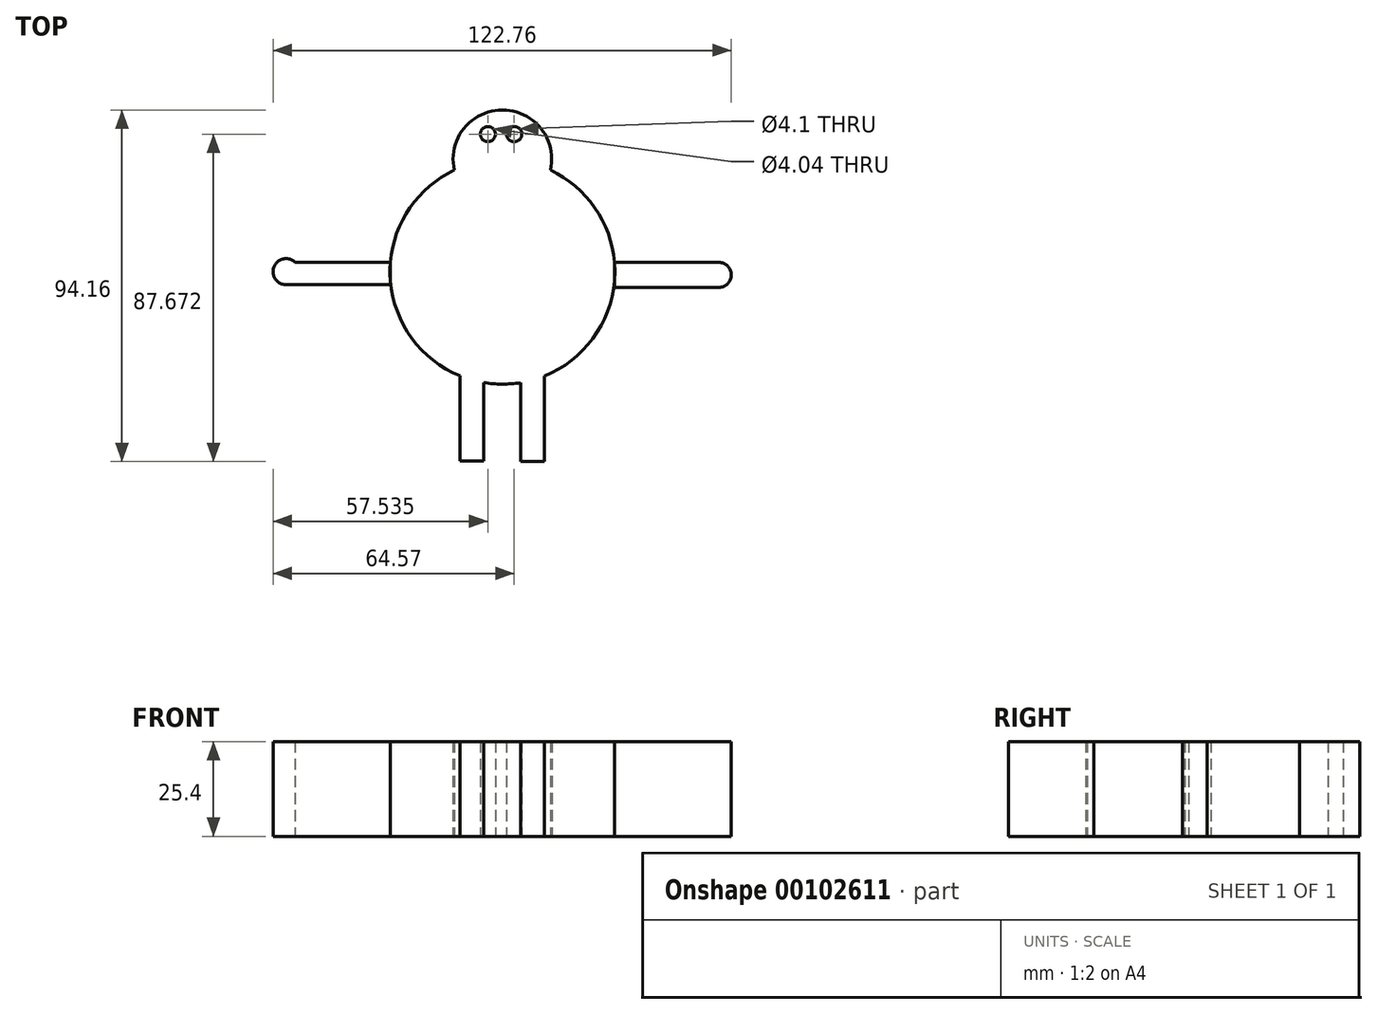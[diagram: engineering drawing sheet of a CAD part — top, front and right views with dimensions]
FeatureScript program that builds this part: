
annotation { "Feature Type Name" : "Feature", "Feature Type Description" : "" }
export const myFeature = defineFeature(function(context is Context, id is Id, definition is map)
    precondition{}
    {
        {
            var Q0;
            Q0=qCreatedBy(makeId("Top.planeOp"),FACE);
            var sketch = newSketch(context, id + "F0", { "sketchPlane" : qUnion([Q0])});
            skCircle(sketch, "E0", {"center": v(0, 0) * mm, "radius": 30.12 * mm});
            skCircle(sketch, "E1", {"center": v(0, 30.12) * mm, "radius": 13.21 * mm});
            skLineSegment(sketch, "E2.bottom", {"start": v(-30.02, 2.48) * mm, "end": v(-57.96, 2.48) * mm});
            skLineSegment(sketch, "E2.top", {"start": v(-30.02, -3.48) * mm, "end": v(-57.96, -3.48) * mm});
            skLineSegment(sketch, "E2.left", {"start": v(-30.02, 2.48) * mm, "end": v(-30.02, -3.48) * mm});
            skLineSegment(sketch, "E2.right", {"start": v(-57.96, 2.48) * mm, "end": v(-57.96, -3.48) * mm});
            skLineSegment(sketch, "E3.bottom", {"start": v(30.02, 2.48) * mm, "end": v(57.96, 2.48) * mm});
            skLineSegment(sketch, "E3.top", {"start": v(30.02, -4.23) * mm, "end": v(57.96, -4.23) * mm});
            skLineSegment(sketch, "E3.left", {"start": v(30.02, 2.48) * mm, "end": v(30.02, -4.23) * mm});
            skLineSegment(sketch, "E3.right", {"start": v(57.96, 2.48) * mm, "end": v(57.96, -4.23) * mm});
            skCircle(sketch, "E4", {"center": v(57.96, -0.87) * mm, "radius": 3.36 * mm});
            skCircle(sketch, "E5", {"center": v(-57.96, 0) * mm, "radius": 3.48 * mm});
            skLineSegment(sketch, "E6", {"start": v(-57.96, -3.48) * mm, "end": v(-60.96, -9.14) * mm});
            skLineSegment(sketch, "E7", {"start": v(-61.44, 0) * mm, "end": v(-67.56, -6.31) * mm});
            skPoint(sketch, "E7.endSnap0", {"position": v(-59.46, -6.31) * mm});
            skLineSegment(sketch, "E8", {"start": v(-61.44, 2.48) * mm, "end": v(-66.3, 5.59) * mm});
            skLineSegment(sketch, "E9", {"start": v(-57.96, 2.48) * mm, "end": v(-61.98, 11.43) * mm});
            skLineSegment(sketch, "E10", {"start": v(59.5, -3.85) * mm, "end": v(67.3, -11.43) * mm});
            skLineSegment(sketch, "E11", {"start": v(67.3, -11.43) * mm, "end": v(59.5, -3.85) * mm});
            skLineSegment(sketch, "E12", {"start": v(61.2, 0) * mm, "end": v(72.64, -7.87) * mm});
            skLineSegment(sketch, "E13", {"start": v(72.64, -7.87) * mm, "end": v(61.2, 0) * mm});
            skLineSegment(sketch, "E14", {"start": v(61.2, 0) * mm, "end": v(70.87, 6.86) * mm});
            skLineSegment(sketch, "E15", {"start": v(70.87, 6.86) * mm, "end": v(61.2, 0) * mm});
            skLineSegment(sketch, "E16", {"start": v(57.96, 2.48) * mm, "end": v(64.26, 12.2) * mm});
            skLineSegment(sketch, "E17", {"start": v(64.26, 12.2) * mm, "end": v(57.96, 2.48) * mm});
            skLineSegment(sketch, "E18.bottom", {"start": v(-11.35, -27.9) * mm, "end": v(-5, -27.9) * mm});
            skLineSegment(sketch, "E18.top", {"start": v(-11.35, -50.76) * mm, "end": v(-5, -50.76) * mm});
            skLineSegment(sketch, "E18.left", {"start": v(-11.35, -27.9) * mm, "end": v(-11.35, -50.76) * mm});
            skLineSegment(sketch, "E18.right", {"start": v(-5, -27.9) * mm, "end": v(-5, -50.76) * mm});
            skLineSegment(sketch, "E19.bottom", {"start": v(11.19, -27.97) * mm, "end": v(4.84, -27.97) * mm});
            skLineSegment(sketch, "E19.top", {"start": v(11.19, -50.83) * mm, "end": v(4.84, -50.83) * mm});
            skLineSegment(sketch, "E19.left", {"start": v(11.19, -27.97) * mm, "end": v(11.19, -50.83) * mm});
            skLineSegment(sketch, "E19.right", {"start": v(4.84, -27.97) * mm, "end": v(4.84, -50.83) * mm});
            skCircle(sketch, "E20", {"center": v(-3.9, 36.84) * mm, "radius": 2.02 * mm});
            skCircle(sketch, "E21", {"center": v(3.13, 36.84) * mm, "radius": 2.05 * mm});
            skArc(sketch, "E22", {"start": v(-6.28, 29.46) * mm, "mid": v(-0.23, 23.1) * mm, "end": v(5.7, 29.58) * mm});
            skSolve(sketch);
        }
        {
            var Q0;
            {var subQ0=sQuery(id+"F0.wireOp",EDGE,"E18.bottom");Q0=makeQuery(id+"F0.imprint","IMPRINT",FACE,{"disambiguationData":[TD([[makeQuery(id+"F0.imprint","IMPRINT",EDGE,{"derivedFrom":subQ0}),1.0]])]});}
            var Q1;
            Q1=makeQuery(id+"F0.imprint","IMPRINT",FACE,{"disambiguationData":[TD([[makeQuery(id+"F0.imprint","IMPRINT",EDGE,{"derivedFrom":sQuery(id+"F0.wireOp",EDGE,"E20")}),-1.0]])]});
            var Q2;
            {var subQ0=sQuery(id+"F0.wireOp",EDGE,"E22");Q2=makeQuery(id+"F0.imprint","IMPRINT",FACE,{"disambiguationData":[TD([[makeQuery(id+"F0.imprint","IMPRINT",EDGE,{"derivedFrom":subQ0}),-1.0]])]});}
            var Q3;
            {var subQ0=sQuery(id+"F0.wireOp",EDGE,"E22");Q3=makeQuery(id+"F0.imprint","IMPRINT",FACE,{"disambiguationData":[TD([[makeQuery(id+"F0.imprint","IMPRINT",EDGE,{"derivedFrom":subQ0}),1.0]])]});}
            var Q4;
            {var subQ4=sQuery(id+"F0.wireOp",EDGE,"E3.bottom");Q4=makeQuery(id+"F0.imprint","IMPRINT",FACE,{"disambiguationData":[TD([[makeQuery(id+"F0.imprint","IMPRINT",EDGE,{"derivedFrom":subQ4}),-1.0]])]});}
            var Q5;
            {var subQ0=sQuery(id+"F0.wireOp",EDGE,"E3.right");Q5=makeQuery(id+"F0.imprint","IMPRINT",FACE,{"disambiguationData":[TD([[makeQuery(id+"F0.imprint","IMPRINT",EDGE,{"derivedFrom":subQ0}),-1.0]])]});}
            var Q6;
            {var subQ0=sQuery(id+"F0.wireOp",EDGE,"E3.right");Q6=makeQuery(id+"F0.imprint","IMPRINT",FACE,{"disambiguationData":[TD([[makeQuery(id+"F0.imprint","IMPRINT",EDGE,{"derivedFrom":subQ0}),1.0]])]});}
            var Q7;
            {var subQ4=sQuery(id+"F0.wireOp",EDGE,"E18.top");Q7=makeQuery(id+"F0.imprint","IMPRINT",FACE,{"disambiguationData":[TD([[makeQuery(id+"F0.imprint","IMPRINT",EDGE,{"derivedFrom":subQ4}),1.0]])]});}
            var Q8;
            {var subQ4=sQuery(id+"F0.wireOp",EDGE,"E19.top");Q8=makeQuery(id+"F0.imprint","IMPRINT",FACE,{"disambiguationData":[TD([[makeQuery(id+"F0.imprint","IMPRINT",EDGE,{"derivedFrom":subQ4}),-1.0]])]});}
            var Q9;
            {var subQ1=sQuery(id+"F0.wireOp",EDGE,"E2.top");Q9=makeQuery(id+"F0.imprint","IMPRINT",FACE,{"disambiguationData":[TD([[makeQuery(id+"F0.imprint","IMPRINT",EDGE,{"derivedFrom":subQ1}),-1.0]])]});}
            var Q10;
            {var subQ0=sQuery(id+"F0.wireOp",EDGE,"E2.right");Q10=makeQuery(id+"F0.imprint","IMPRINT",FACE,{"disambiguationData":[TD([[makeQuery(id+"F0.imprint","IMPRINT",EDGE,{"derivedFrom":subQ0}),-1.0]])]});}
            var Q11;
            {var subQ0=sQuery(id+"F0.wireOp",EDGE,"E2.right");Q11=makeQuery(id+"F0.imprint","IMPRINT",FACE,{"disambiguationData":[TD([[makeQuery(id+"F0.imprint","IMPRINT",EDGE,{"derivedFrom":subQ0}),1.0]])]});}
            var Q12;
            {var subQ0=sQuery(id+"F0.wireOp",EDGE,"E19.bottom");Q12=makeQuery(id+"F0.imprint","IMPRINT",FACE,{"disambiguationData":[TD([[makeQuery(id+"F0.imprint","IMPRINT",EDGE,{"derivedFrom":subQ0}),1.0]])]});}
            var Q13;
            {var subQ0=sQuery(id+"F0.wireOp",EDGE,"E18.bottom");Q13=makeQuery(id+"F0.imprint","IMPRINT",FACE,{"disambiguationData":[TD([[makeQuery(id+"F0.imprint","IMPRINT",EDGE,{"derivedFrom":subQ0}),-1.0]])]});}
            var Q14;
            {var subQ0=sQuery(id+"F0.wireOp",EDGE,"E9");var subQ3=sQuery(id+"F0.wireOp",EDGE,"E5");var subQ5=makeQuery(id+"F0.imprint","INTERSECT",VERTEX,{"derivedFrom":[subQ3,subQ0]});Q14=makeQuery(id+"F0.imprint","IMPRINT",FACE,{"disambiguationData":[TD([[makeQuery(id+"F0.imprint","IMPRINT",EDGE,{"disambiguationData":[TD([[subQ5,1.0]])],"derivedFrom":subQ3}),1.0]])]});}
            extrude(context, id + "F1", {"entities" : qUnion([Q0, Q1, Q2, Q3, Q4, Q5, Q6, Q7, Q8, Q9, Q10, Q11, Q12, Q13, Q14]), "depth" : 25.4 * mm});
        }
    });
